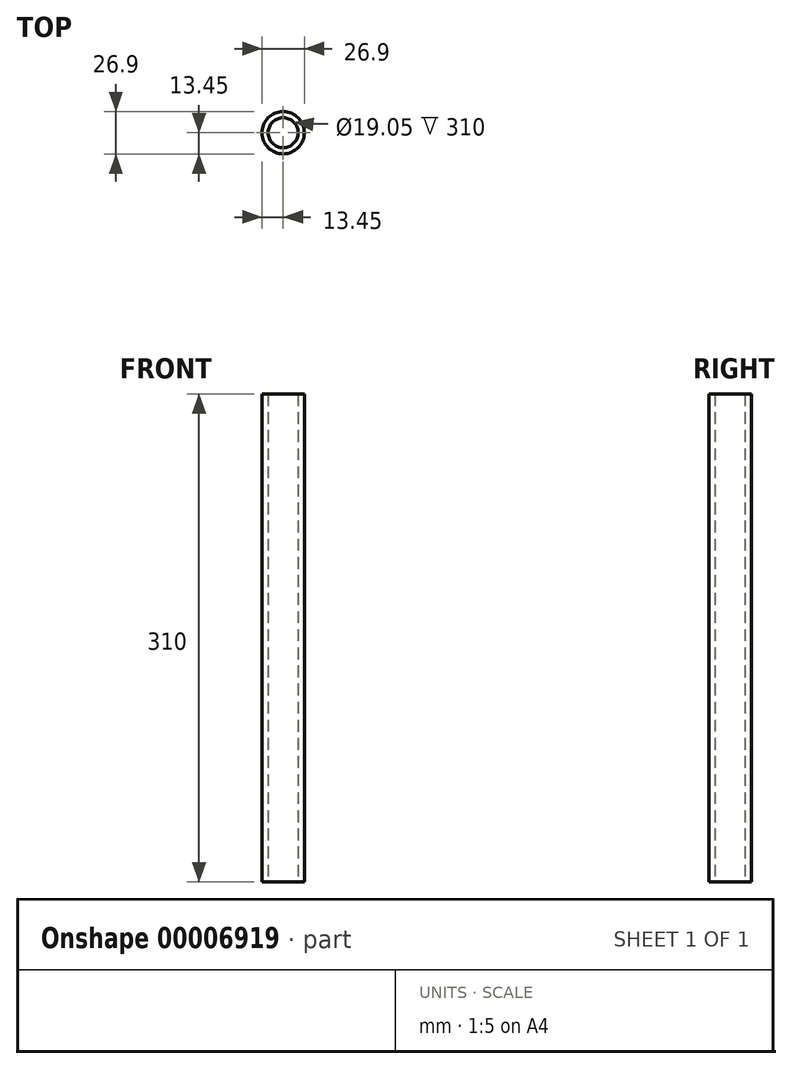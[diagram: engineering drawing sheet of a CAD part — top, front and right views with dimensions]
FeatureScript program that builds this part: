
annotation { "Feature Type Name" : "Feature", "Feature Type Description" : "" }
export const myFeature = defineFeature(function(context is Context, id is Id, definition is map)
    precondition{}
    {
        {
            var Q0;
            Q0=qCreatedBy(makeId("Top.planeOp"),FACE);
            var sketch = newSketch(context, id + "F0", { "sketchPlane" : qUnion([Q0])});
            skCircle(sketch, "E0", {"center": v(0, 0) * mm, "radius": 13.45 * mm});
            skCircle(sketch, "E1", {"center": v(0, 0) * mm, "radius": 9.53 * mm});
            skSolve(sketch);
        }
        {
            var Q0;
            Q0=makeQuery(id+"F0.imprint","IMPRINT",FACE,{"disambiguationData":[TD([[makeQuery(id+"F0.imprint","IMPRINT",EDGE,{"derivedFrom":sQuery(id+"F0.wireOp",EDGE,"E0")}),1.0]])]});
            extrude(context, id + "F1", {"entities" : qUnion([Q0]), "depth" : 310 * mm});
        }
    });
